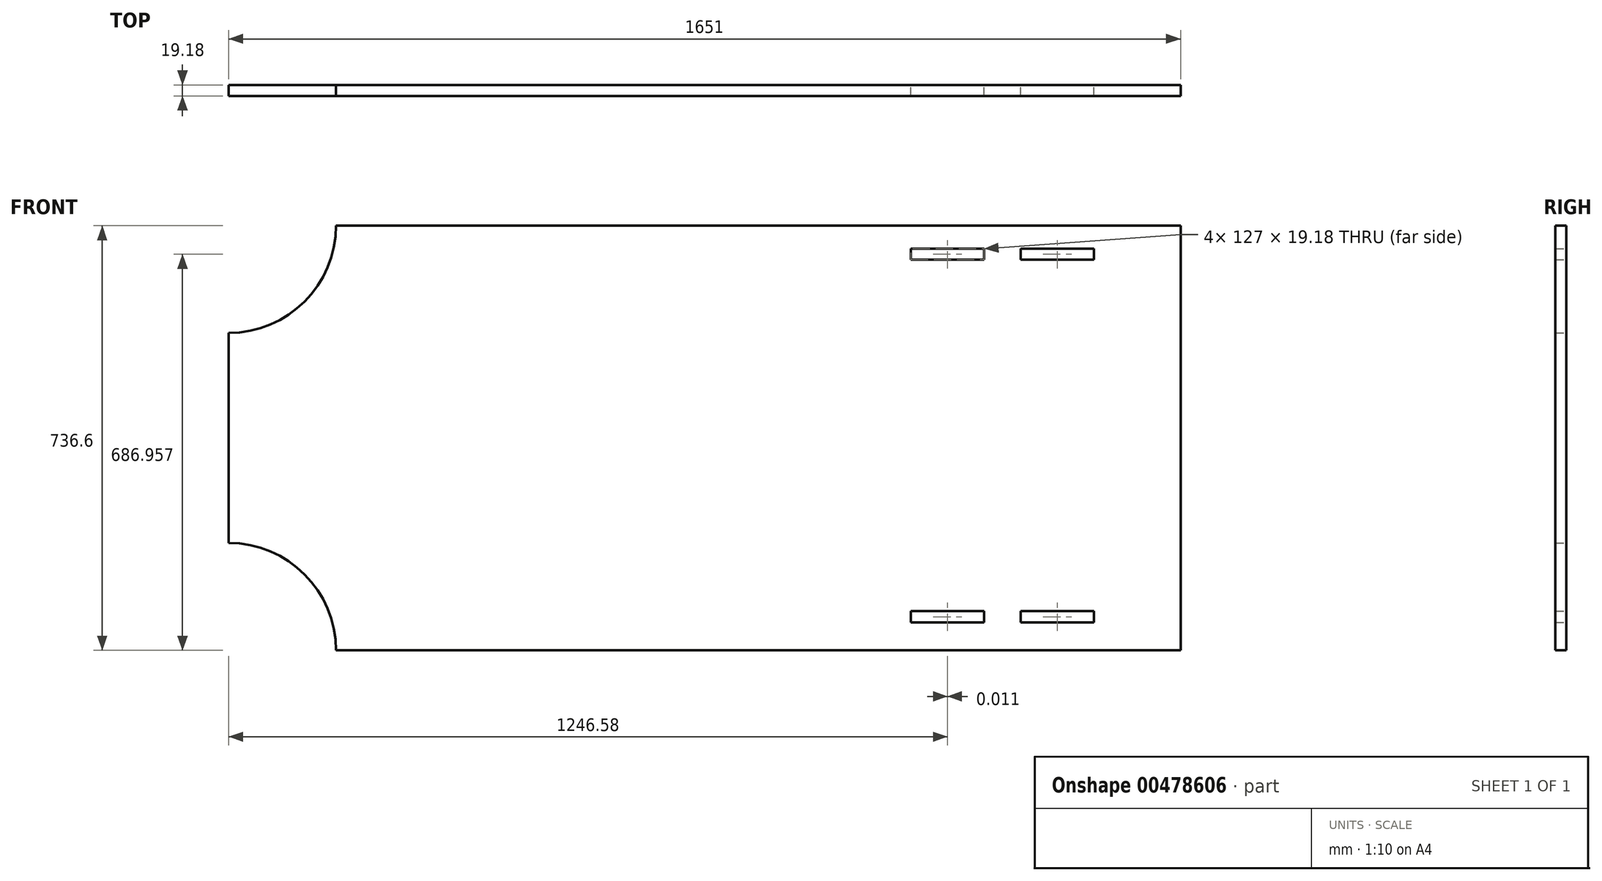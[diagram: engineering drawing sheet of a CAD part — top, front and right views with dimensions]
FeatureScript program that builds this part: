
annotation { "Feature Type Name" : "Feature", "Feature Type Description" : "" }
export const myFeature = defineFeature(function(context is Context, id is Id, definition is map)
    precondition{}
    {
        {
            var Q0;
            Q0=qCreatedBy(makeId("Front.planeOp"),FACE);
            var sketch = newSketch(context, id + "F0", { "sketchPlane" : qUnion([Q0])});
            skLineSegment(sketch, "E0.bottom", {"start": v(-823.86, 380.3) * mm, "end": v(640.88, 380.3) * mm});
            skLineSegment(sketch, "E0.top", {"start": v(-823.86, -356.3) * mm, "end": v(640.88, -356.3) * mm});
            skLineSegment(sketch, "E0.right", {"start": v(640.88, 380.3) * mm, "end": v(640.88, -356.3) * mm});
            skLineSegment(sketch, "E1", {"start": v(363.47, -307.7) * mm, "end": v(363.47, -288.53) * mm});
            skLineSegment(sketch, "E2", {"start": v(490.47, -307.7) * mm, "end": v(490.47, -288.53) * mm});
            skLineSegment(sketch, "E3", {"start": v(299.97, -307.7) * mm, "end": v(299.97, -288.53) * mm});
            skLineSegment(sketch, "E4", {"start": v(172.97, -307.7) * mm, "end": v(172.97, -288.53) * mm});
            skLineSegment(sketch, "E5", {"start": v(172.97, -307.7) * mm, "end": v(299.97, -307.7) * mm});
            skLineSegment(sketch, "E6", {"start": v(363.47, -307.7) * mm, "end": v(490.47, -307.7) * mm});
            skLineSegment(sketch, "E7", {"start": v(172.97, -288.53) * mm, "end": v(299.97, -288.53) * mm});
            skLineSegment(sketch, "E8", {"start": v(363.47, -288.53) * mm, "end": v(490.47, -288.53) * mm});
            skLineSegment(sketch, "E9.bottom", {"start": v(490.46, 321.07) * mm, "end": v(363.46, 321.07) * mm});
            skLineSegment(sketch, "E9.top", {"start": v(490.46, 340.25) * mm, "end": v(363.46, 340.25) * mm});
            skLineSegment(sketch, "E9.left", {"start": v(490.46, 321.07) * mm, "end": v(490.46, 340.25) * mm});
            skLineSegment(sketch, "E9.right", {"start": v(363.46, 321.07) * mm, "end": v(363.46, 340.25) * mm});
            skLineSegment(sketch, "E10.bottom", {"start": v(299.96, 321.07) * mm, "end": v(172.96, 321.07) * mm});
            skLineSegment(sketch, "E10.top", {"start": v(299.96, 340.25) * mm, "end": v(172.96, 340.25) * mm});
            skLineSegment(sketch, "E10.left", {"start": v(299.96, 321.07) * mm, "end": v(299.96, 340.25) * mm});
            skLineSegment(sketch, "E10.right", {"start": v(172.96, 321.07) * mm, "end": v(172.96, 340.25) * mm});
            skLineSegment(sketch, "E11", {"start": v(-1010.12, -170.04) * mm, "end": v(-1010.12, 194.04) * mm});
            skPoint(sketch, "E12.center.orphan", {"position": v(-1010.12, 380.3) * mm});
            skPoint(sketch, "E13.center.orphan", {"position": v(-1010.12, -356.3) * mm});
            skArc(sketch, "E14", {"start": v(-1010.12, 194.04) * mm, "mid": v(-878.42, 248.6) * mm, "end": v(-823.86, 380.3) * mm});
            skArc(sketch, "E15", {"start": v(-823.86, -356.3) * mm, "mid": v(-878.42, -224.6) * mm, "end": v(-1010.12, -170.04) * mm});
            skPoint(sketch, "E16.start.orphan", {"position": v(-951.82, -356.3) * mm});
            skLineSegment(sketch, "E17", {"start": v(299.96, 321.07) * mm, "end": v(363.46, 321.07) * mm, "construction": true});
            skSolve(sketch);
        }
        {
            var Q0;
            Q0 = qSketchRegion(id + "F0", true);
            extrude(context, id + "F1", {"entities" : qUnion([Q0]), "depth" : 19.18 * mm, "offsetDistance" : 25.4 * mm});
        }
    });
